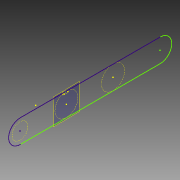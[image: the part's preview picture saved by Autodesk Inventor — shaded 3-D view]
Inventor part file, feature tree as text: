
AUTODESK INVENTOR PART (.ipt)
format: ipt  version: 2015 (Build 190159000, 159)  size: 89,600 bytes
history: native  units: in
note: dims shown in document units (in); Inventor stores cm internally (conversion verified against a paired STEP export)
features: other x45, reference x6, sketch x2, plane x1, pattern_linear x1
ambient origin geometry x8: Origin, YZ Plane, XZ Plane, XY Plane, X Axis, Y Axis, Z Axis, Center Point
feature tree (55):
  plane  "Work Plane1"
  sketch  "Sketch1"  dims[d2=17.5473in]
  sketch  "Sketch3"
  other  "Work Point42"
  pattern_linear  "Rectangular Pattern2"  [2 undecoded]
  reference  "Reference1"
  reference  "Reference2"
  reference  "Reference3"
  reference  "Reference5"
  reference  "Reference6"
  reference  "Reference7"
  other  "Work Point43"
  other  "Work Point44"
  other  "Work Point45"
  other  "Work Point46"
  other  "Work Point47"
  other  "Work Point48"
  other  "Work Point49"
  other  "Work Point50"
  other  "Work Point51"
  other  "Work Point52"
  other  "Work Point53"
  other  "Work Point54"
  other  "Work Point55"
  other  "Work Point56"
  other  "Work Point57"
  other  "Work Point58"
  other  "Work Point59"
  other  "Work Point60"
  other  "Work Point61"
  other  "Work Point62"
  other  "Work Point63"
  other  "Work Point64"
  other  "Work Point65"
  other  "Work Point66"
  other  "Work Point67"
  other  "Work Point68"
  other  "Work Point69"
  other  "Work Point70"
  other  "Work Point71"
  other  "Work Point72"
  other  "Work Point73"
  other  "Work Point74"
  other  "Work Point75"
  other  "Work Point76"
  other  "Work Point77"
  other  "Work Point78"
  other  "Work Point79"
  other  "Work Point80"
  other  "Work Point81"
  other  "Work Point82"
  other  "Work Point83"
  other  "Work Point84"
  other  "Work Point85"
  other  "Work Point86"
note: 2 required parameter values undecoded (feature->parameter linkage not recoverable at this tier; creation-order binding heuristic only, values carry confidence <= 0.55)
